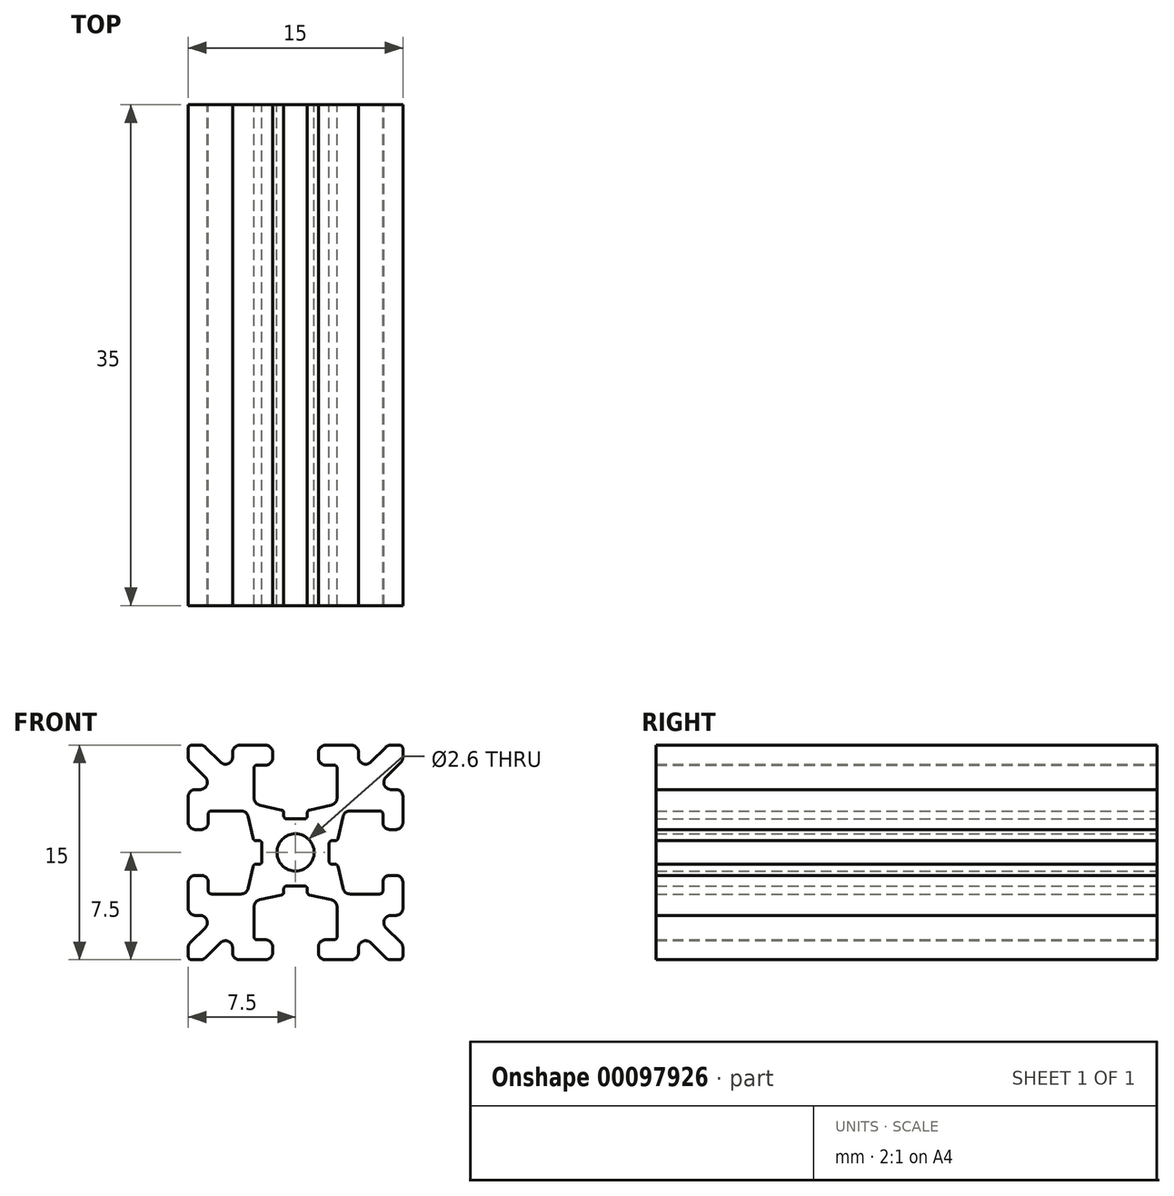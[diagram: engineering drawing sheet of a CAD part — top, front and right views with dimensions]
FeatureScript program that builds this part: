
annotation { "Feature Type Name" : "Feature", "Feature Type Description" : "" }
export const myFeature = defineFeature(function(context is Context, id is Id, definition is map)
    precondition{}
    {
        {
            var Q0;
            Q0=qCreatedBy(makeId("Front.planeOp"),FACE);
            var sketch = newSketch(context, id + "F0", { "sketchPlane" : qUnion([Q0])});
            skLineSegment(sketch, "E0.0.0", {"start": v(0.83, -2.55) * mm, "end": v(0.83, -2.77) * mm});
            skArc(sketch, "E0.0.1", {"start": v(0.83, -2.77) * mm, "mid": v(0.87, -2.9) * mm, "end": v(0.98, -2.97) * mm});
            skLineSegment(sketch, "E0.0.2", {"start": v(0.98, -2.97) * mm, "end": v(2.5, -3.31) * mm});
            skArc(sketch, "E0.0.3", {"start": v(2.5, -3.31) * mm, "mid": v(2.8, -3.49) * mm, "end": v(2.9, -3.8) * mm});
            skLineSegment(sketch, "E0.0.4", {"start": v(2.9, -3.8) * mm, "end": v(2.9, -5.9) * mm});
            skArc(sketch, "E0.0.5", {"start": v(2.9, -5.9) * mm, "mid": v(2.84, -6.04) * mm, "end": v(2.7, -6.1) * mm});
            skLineSegment(sketch, "E0.0.6", {"start": v(2.7, -6.1) * mm, "end": v(2.1, -6.1) * mm});
            skArc(sketch, "E0.0.7", {"start": v(2.1, -6.1) * mm, "mid": v(1.75, -6.25) * mm, "end": v(1.6, -6.6) * mm});
            skLineSegment(sketch, "E0.0.8", {"start": v(1.6, -6.6) * mm, "end": v(1.6, -7) * mm});
            skArc(sketch, "E0.0.9", {"start": v(1.6, -7) * mm, "mid": v(1.75, -7.35) * mm, "end": v(2.1, -7.5) * mm});
            skLineSegment(sketch, "E0.0.10", {"start": v(2.1, -7.5) * mm, "end": v(3.9, -7.5) * mm});
            skArc(sketch, "E0.0.11", {"start": v(3.9, -7.5) * mm, "mid": v(4.25, -7.35) * mm, "end": v(4.4, -7) * mm});
            skLineSegment(sketch, "E0.0.12", {"start": v(4.4, -7) * mm, "end": v(4.4, -6.67) * mm});
            skArc(sketch, "E0.0.13", {"start": v(4.4, -6.67) * mm, "mid": v(4.7, -6.2) * mm, "end": v(5.25, -6.31) * mm});
            skLineSegment(sketch, "E0.0.14", {"start": v(5.25, -6.31) * mm, "end": v(6.3, -7.35) * mm});
            skArc(sketch, "E0.0.15", {"start": v(6.3, -7.35) * mm, "mid": v(6.46, -7.46) * mm, "end": v(6.65, -7.5) * mm});
            skLineSegment(sketch, "E0.0.16", {"start": v(6.65, -7.5) * mm, "end": v(7.25, -7.5) * mm});
            skArc(sketch, "E0.0.17", {"start": v(7.25, -7.5) * mm, "mid": v(7.43, -7.43) * mm, "end": v(7.5, -7.25) * mm});
            skLineSegment(sketch, "E0.0.18", {"start": v(7.5, -7.25) * mm, "end": v(7.5, -6.65) * mm});
            skArc(sketch, "E0.0.19", {"start": v(7.5, -6.65) * mm, "mid": v(7.46, -6.46) * mm, "end": v(7.35, -6.3) * mm});
            skLineSegment(sketch, "E0.0.20", {"start": v(7.35, -6.3) * mm, "end": v(6.31, -5.25) * mm});
            skArc(sketch, "E0.0.21", {"start": v(6.31, -5.25) * mm, "mid": v(6.2, -4.7) * mm, "end": v(6.67, -4.4) * mm});
            skLineSegment(sketch, "E0.0.22", {"start": v(6.67, -4.4) * mm, "end": v(7, -4.4) * mm});
            skArc(sketch, "E0.0.23", {"start": v(7, -4.4) * mm, "mid": v(7.35, -4.25) * mm, "end": v(7.5, -3.9) * mm});
            skLineSegment(sketch, "E0.0.24", {"start": v(7.5, -3.9) * mm, "end": v(7.5, -2.1) * mm});
            skArc(sketch, "E0.0.25", {"start": v(7.5, -2.1) * mm, "mid": v(7.35, -1.75) * mm, "end": v(7, -1.6) * mm});
            skLineSegment(sketch, "E0.0.26", {"start": v(7, -1.6) * mm, "end": v(6.6, -1.6) * mm});
            skArc(sketch, "E0.0.27", {"start": v(6.6, -1.6) * mm, "mid": v(6.25, -1.75) * mm, "end": v(6.1, -2.1) * mm});
            skLineSegment(sketch, "E0.0.28", {"start": v(6.1, -2.1) * mm, "end": v(6.1, -2.7) * mm});
            skArc(sketch, "E0.0.29", {"start": v(6.1, -2.7) * mm, "mid": v(6.04, -2.84) * mm, "end": v(5.9, -2.9) * mm});
            skLineSegment(sketch, "E0.0.30", {"start": v(5.9, -2.9) * mm, "end": v(3.8, -2.9) * mm});
            skArc(sketch, "E0.0.31", {"start": v(3.8, -2.9) * mm, "mid": v(3.49, -2.8) * mm, "end": v(3.31, -2.5) * mm});
            skLineSegment(sketch, "E0.0.32", {"start": v(3.31, -2.5) * mm, "end": v(2.97, -0.98) * mm});
            skArc(sketch, "E0.0.33", {"start": v(2.97, -0.98) * mm, "mid": v(2.9, -0.87) * mm, "end": v(2.77, -0.83) * mm});
            skLineSegment(sketch, "E0.0.34", {"start": v(2.77, -0.83) * mm, "end": v(2.55, -0.83) * mm});
            skArc(sketch, "E0.0.35", {"start": v(2.55, -0.83) * mm, "mid": v(2.4, -0.77) * mm, "end": v(2.35, -0.63) * mm});
            skLineSegment(sketch, "E0.0.36", {"start": v(2.35, -0.63) * mm, "end": v(2.35, 0.63) * mm});
            skArc(sketch, "E0.0.37", {"start": v(2.35, 0.63) * mm, "mid": v(2.4, 0.77) * mm, "end": v(2.55, 0.83) * mm});
            skLineSegment(sketch, "E0.0.38", {"start": v(2.55, 0.83) * mm, "end": v(2.77, 0.83) * mm});
            skArc(sketch, "E0.0.39", {"start": v(2.77, 0.83) * mm, "mid": v(2.9, 0.87) * mm, "end": v(2.97, 0.98) * mm});
            skLineSegment(sketch, "E0.0.40", {"start": v(2.97, 0.98) * mm, "end": v(3.31, 2.5) * mm});
            skArc(sketch, "E0.0.41", {"start": v(3.31, 2.5) * mm, "mid": v(3.49, 2.8) * mm, "end": v(3.8, 2.9) * mm});
            skLineSegment(sketch, "E0.0.42", {"start": v(3.8, 2.9) * mm, "end": v(5.9, 2.9) * mm});
            skArc(sketch, "E0.0.43", {"start": v(5.9, 2.9) * mm, "mid": v(6.04, 2.84) * mm, "end": v(6.1, 2.7) * mm});
            skLineSegment(sketch, "E0.0.44", {"start": v(6.1, 2.7) * mm, "end": v(6.1, 2.1) * mm});
            skArc(sketch, "E0.0.45", {"start": v(6.1, 2.1) * mm, "mid": v(6.25, 1.75) * mm, "end": v(6.6, 1.6) * mm});
            skLineSegment(sketch, "E0.0.46", {"start": v(6.6, 1.6) * mm, "end": v(7, 1.6) * mm});
            skArc(sketch, "E0.0.47", {"start": v(7, 1.6) * mm, "mid": v(7.35, 1.75) * mm, "end": v(7.5, 2.1) * mm});
            skLineSegment(sketch, "E0.0.48", {"start": v(7.5, 2.1) * mm, "end": v(7.5, 3.9) * mm});
            skArc(sketch, "E0.0.49", {"start": v(7.5, 3.9) * mm, "mid": v(7.35, 4.25) * mm, "end": v(7, 4.4) * mm});
            skLineSegment(sketch, "E0.0.50", {"start": v(7, 4.4) * mm, "end": v(6.67, 4.4) * mm});
            skArc(sketch, "E0.0.51", {"start": v(6.67, 4.4) * mm, "mid": v(6.2, 4.7) * mm, "end": v(6.31, 5.25) * mm});
            skLineSegment(sketch, "E0.0.52", {"start": v(6.31, 5.25) * mm, "end": v(7.35, 6.3) * mm});
            skArc(sketch, "E0.0.53", {"start": v(7.35, 6.3) * mm, "mid": v(7.46, 6.46) * mm, "end": v(7.5, 6.65) * mm});
            skLineSegment(sketch, "E0.0.54", {"start": v(7.5, 6.65) * mm, "end": v(7.5, 7.25) * mm});
            skArc(sketch, "E0.0.55", {"start": v(7.5, 7.25) * mm, "mid": v(7.43, 7.43) * mm, "end": v(7.25, 7.5) * mm});
            skLineSegment(sketch, "E0.0.56", {"start": v(7.25, 7.5) * mm, "end": v(6.65, 7.5) * mm});
            skArc(sketch, "E0.0.57", {"start": v(6.65, 7.5) * mm, "mid": v(6.46, 7.46) * mm, "end": v(6.3, 7.35) * mm});
            skLineSegment(sketch, "E0.0.58", {"start": v(6.3, 7.35) * mm, "end": v(5.25, 6.31) * mm});
            skArc(sketch, "E0.0.59", {"start": v(5.25, 6.31) * mm, "mid": v(4.7, 6.2) * mm, "end": v(4.4, 6.67) * mm});
            skLineSegment(sketch, "E0.0.60", {"start": v(4.4, 6.67) * mm, "end": v(4.4, 7) * mm});
            skArc(sketch, "E0.0.61", {"start": v(4.4, 7) * mm, "mid": v(4.25, 7.35) * mm, "end": v(3.9, 7.5) * mm});
            skLineSegment(sketch, "E0.0.62", {"start": v(3.9, 7.5) * mm, "end": v(2.1, 7.5) * mm});
            skArc(sketch, "E0.0.63", {"start": v(2.1, 7.5) * mm, "mid": v(1.75, 7.35) * mm, "end": v(1.6, 7) * mm});
            skLineSegment(sketch, "E0.0.64", {"start": v(1.6, 7) * mm, "end": v(1.6, 6.6) * mm});
            skArc(sketch, "E0.0.65", {"start": v(1.6, 6.6) * mm, "mid": v(1.75, 6.25) * mm, "end": v(2.1, 6.1) * mm});
            skLineSegment(sketch, "E0.0.66", {"start": v(2.1, 6.1) * mm, "end": v(2.7, 6.1) * mm});
            skArc(sketch, "E0.0.67", {"start": v(2.7, 6.1) * mm, "mid": v(2.84, 6.04) * mm, "end": v(2.9, 5.9) * mm});
            skLineSegment(sketch, "E0.0.68", {"start": v(2.9, 5.9) * mm, "end": v(2.9, 3.8) * mm});
            skArc(sketch, "E0.0.69", {"start": v(2.9, 3.8) * mm, "mid": v(2.8, 3.49) * mm, "end": v(2.5, 3.31) * mm});
            skLineSegment(sketch, "E0.0.70", {"start": v(2.5, 3.31) * mm, "end": v(0.98, 2.97) * mm});
            skArc(sketch, "E0.0.71", {"start": v(0.98, 2.97) * mm, "mid": v(0.87, 2.9) * mm, "end": v(0.83, 2.77) * mm});
            skLineSegment(sketch, "E0.0.72", {"start": v(0.83, 2.77) * mm, "end": v(0.83, 2.55) * mm});
            skArc(sketch, "E0.0.73", {"start": v(0.83, 2.55) * mm, "mid": v(0.77, 2.4) * mm, "end": v(0.63, 2.35) * mm});
            skLineSegment(sketch, "E0.0.74", {"start": v(0.63, 2.35) * mm, "end": v(-0.63, 2.35) * mm});
            skArc(sketch, "E0.0.75", {"start": v(-0.63, 2.35) * mm, "mid": v(-0.77, 2.4) * mm, "end": v(-0.83, 2.55) * mm});
            skLineSegment(sketch, "E0.0.76", {"start": v(-0.83, 2.55) * mm, "end": v(-0.83, 2.77) * mm});
            skArc(sketch, "E0.0.77", {"start": v(-0.83, 2.77) * mm, "mid": v(-0.87, 2.9) * mm, "end": v(-0.98, 2.97) * mm});
            skLineSegment(sketch, "E0.0.78", {"start": v(-0.98, 2.97) * mm, "end": v(-2.5, 3.31) * mm});
            skArc(sketch, "E0.0.79", {"start": v(-2.5, 3.31) * mm, "mid": v(-2.8, 3.49) * mm, "end": v(-2.9, 3.8) * mm});
            skLineSegment(sketch, "E0.0.80", {"start": v(-2.9, 3.8) * mm, "end": v(-2.9, 5.9) * mm});
            skArc(sketch, "E0.0.81", {"start": v(-2.9, 5.9) * mm, "mid": v(-2.84, 6.04) * mm, "end": v(-2.7, 6.1) * mm});
            skLineSegment(sketch, "E0.0.82", {"start": v(-2.7, 6.1) * mm, "end": v(-2.1, 6.1) * mm});
            skArc(sketch, "E0.0.83", {"start": v(-2.1, 6.1) * mm, "mid": v(-1.75, 6.25) * mm, "end": v(-1.6, 6.6) * mm});
            skLineSegment(sketch, "E0.0.84", {"start": v(-1.6, 6.6) * mm, "end": v(-1.6, 7) * mm});
            skArc(sketch, "E0.0.85", {"start": v(-1.6, 7) * mm, "mid": v(-1.75, 7.35) * mm, "end": v(-2.1, 7.5) * mm});
            skLineSegment(sketch, "E0.0.86", {"start": v(-2.1, 7.5) * mm, "end": v(-3.9, 7.5) * mm});
            skArc(sketch, "E0.0.87", {"start": v(-3.9, 7.5) * mm, "mid": v(-4.25, 7.35) * mm, "end": v(-4.4, 7) * mm});
            skLineSegment(sketch, "E0.0.88", {"start": v(-4.4, 7) * mm, "end": v(-4.4, 6.67) * mm});
            skArc(sketch, "E0.0.89", {"start": v(-4.4, 6.67) * mm, "mid": v(-4.7, 6.2) * mm, "end": v(-5.25, 6.31) * mm});
            skLineSegment(sketch, "E0.0.90", {"start": v(-5.25, 6.31) * mm, "end": v(-6.3, 7.35) * mm});
            skArc(sketch, "E0.0.91", {"start": v(-6.3, 7.35) * mm, "mid": v(-6.46, 7.46) * mm, "end": v(-6.65, 7.5) * mm});
            skLineSegment(sketch, "E0.0.92", {"start": v(-6.65, 7.5) * mm, "end": v(-7.25, 7.5) * mm});
            skArc(sketch, "E0.0.93", {"start": v(-7.25, 7.5) * mm, "mid": v(-7.43, 7.43) * mm, "end": v(-7.5, 7.25) * mm});
            skLineSegment(sketch, "E0.0.94", {"start": v(-7.5, 7.25) * mm, "end": v(-7.5, 6.65) * mm});
            skArc(sketch, "E0.0.95", {"start": v(-7.5, 6.65) * mm, "mid": v(-7.46, 6.46) * mm, "end": v(-7.35, 6.3) * mm});
            skLineSegment(sketch, "E0.0.96", {"start": v(-7.35, 6.3) * mm, "end": v(-6.31, 5.25) * mm});
            skArc(sketch, "E0.0.97", {"start": v(-6.31, 5.25) * mm, "mid": v(-6.2, 4.7) * mm, "end": v(-6.67, 4.4) * mm});
            skLineSegment(sketch, "E0.0.98", {"start": v(-6.67, 4.4) * mm, "end": v(-7, 4.4) * mm});
            skArc(sketch, "E0.0.99", {"start": v(-7, 4.4) * mm, "mid": v(-7.35, 4.25) * mm, "end": v(-7.5, 3.9) * mm});
            skLineSegment(sketch, "E0.0.100", {"start": v(-7.5, 3.9) * mm, "end": v(-7.5, 2.1) * mm});
            skArc(sketch, "E0.0.101", {"start": v(-7.5, 2.1) * mm, "mid": v(-7.35, 1.75) * mm, "end": v(-7, 1.6) * mm});
            skLineSegment(sketch, "E0.0.102", {"start": v(-7, 1.6) * mm, "end": v(-6.6, 1.6) * mm});
            skArc(sketch, "E0.0.103", {"start": v(-6.6, 1.6) * mm, "mid": v(-6.25, 1.75) * mm, "end": v(-6.1, 2.1) * mm});
            skLineSegment(sketch, "E0.0.104", {"start": v(-6.1, 2.1) * mm, "end": v(-6.1, 2.7) * mm});
            skArc(sketch, "E0.0.105", {"start": v(-6.1, 2.7) * mm, "mid": v(-6.04, 2.84) * mm, "end": v(-5.9, 2.9) * mm});
            skLineSegment(sketch, "E0.0.106", {"start": v(-5.9, 2.9) * mm, "end": v(-3.8, 2.9) * mm});
            skArc(sketch, "E0.0.107", {"start": v(-3.8, 2.9) * mm, "mid": v(-3.49, 2.8) * mm, "end": v(-3.31, 2.5) * mm});
            skLineSegment(sketch, "E0.0.108", {"start": v(-3.31, 2.5) * mm, "end": v(-2.97, 0.98) * mm});
            skArc(sketch, "E0.0.109", {"start": v(-2.97, 0.98) * mm, "mid": v(-2.9, 0.87) * mm, "end": v(-2.77, 0.83) * mm});
            skLineSegment(sketch, "E0.0.110", {"start": v(-2.77, 0.83) * mm, "end": v(-2.55, 0.83) * mm});
            skArc(sketch, "E0.0.111", {"start": v(-2.55, 0.83) * mm, "mid": v(-2.4, 0.77) * mm, "end": v(-2.35, 0.63) * mm});
            skLineSegment(sketch, "E0.0.112", {"start": v(-2.35, 0.63) * mm, "end": v(-2.35, -0.63) * mm});
            skArc(sketch, "E0.0.113", {"start": v(-2.35, -0.63) * mm, "mid": v(-2.4, -0.77) * mm, "end": v(-2.55, -0.83) * mm});
            skLineSegment(sketch, "E0.0.114", {"start": v(-2.55, -0.83) * mm, "end": v(-2.77, -0.83) * mm});
            skArc(sketch, "E0.0.115", {"start": v(-2.77, -0.83) * mm, "mid": v(-2.9, -0.87) * mm, "end": v(-2.97, -0.98) * mm});
            skLineSegment(sketch, "E0.0.116", {"start": v(-2.97, -0.98) * mm, "end": v(-3.31, -2.5) * mm});
            skArc(sketch, "E0.0.117", {"start": v(-3.31, -2.5) * mm, "mid": v(-3.49, -2.8) * mm, "end": v(-3.8, -2.9) * mm});
            skLineSegment(sketch, "E0.0.118", {"start": v(-3.8, -2.9) * mm, "end": v(-5.9, -2.9) * mm});
            skArc(sketch, "E0.0.119", {"start": v(-5.9, -2.9) * mm, "mid": v(-6.04, -2.84) * mm, "end": v(-6.1, -2.7) * mm});
            skLineSegment(sketch, "E0.0.120", {"start": v(-6.1, -2.7) * mm, "end": v(-6.1, -2.1) * mm});
            skArc(sketch, "E0.0.121", {"start": v(-6.1, -2.1) * mm, "mid": v(-6.25, -1.75) * mm, "end": v(-6.6, -1.6) * mm});
            skLineSegment(sketch, "E0.0.122", {"start": v(-6.6, -1.6) * mm, "end": v(-7, -1.6) * mm});
            skArc(sketch, "E0.0.123", {"start": v(-7, -1.6) * mm, "mid": v(-7.35, -1.75) * mm, "end": v(-7.5, -2.1) * mm});
            skLineSegment(sketch, "E0.0.124", {"start": v(-7.5, -2.1) * mm, "end": v(-7.5, -3.9) * mm});
            skArc(sketch, "E0.0.125", {"start": v(-7.5, -3.9) * mm, "mid": v(-7.35, -4.25) * mm, "end": v(-7, -4.4) * mm});
            skLineSegment(sketch, "E0.0.126", {"start": v(-7, -4.4) * mm, "end": v(-6.67, -4.4) * mm});
            skArc(sketch, "E0.0.127", {"start": v(-6.67, -4.4) * mm, "mid": v(-6.2, -4.7) * mm, "end": v(-6.31, -5.25) * mm});
            skLineSegment(sketch, "E0.0.128", {"start": v(-6.31, -5.25) * mm, "end": v(-7.35, -6.3) * mm});
            skArc(sketch, "E0.0.129", {"start": v(-7.35, -6.3) * mm, "mid": v(-7.46, -6.46) * mm, "end": v(-7.5, -6.65) * mm});
            skLineSegment(sketch, "E0.0.130", {"start": v(-7.5, -6.65) * mm, "end": v(-7.5, -7.25) * mm});
            skArc(sketch, "E0.0.131", {"start": v(-7.5, -7.25) * mm, "mid": v(-7.43, -7.43) * mm, "end": v(-7.25, -7.5) * mm});
            skLineSegment(sketch, "E0.0.132", {"start": v(-7.25, -7.5) * mm, "end": v(-6.65, -7.5) * mm});
            skArc(sketch, "E0.0.133", {"start": v(-6.65, -7.5) * mm, "mid": v(-6.46, -7.46) * mm, "end": v(-6.3, -7.35) * mm});
            skLineSegment(sketch, "E0.0.134", {"start": v(-6.3, -7.35) * mm, "end": v(-5.25, -6.31) * mm});
            skArc(sketch, "E0.0.135", {"start": v(-5.25, -6.31) * mm, "mid": v(-4.7, -6.2) * mm, "end": v(-4.4, -6.67) * mm});
            skLineSegment(sketch, "E0.0.136", {"start": v(-4.4, -6.67) * mm, "end": v(-4.4, -7) * mm});
            skArc(sketch, "E0.0.137", {"start": v(-4.4, -7) * mm, "mid": v(-4.25, -7.35) * mm, "end": v(-3.9, -7.5) * mm});
            skLineSegment(sketch, "E0.0.138", {"start": v(-3.9, -7.5) * mm, "end": v(-2.1, -7.5) * mm});
            skArc(sketch, "E0.0.139", {"start": v(-2.1, -7.5) * mm, "mid": v(-1.75, -7.35) * mm, "end": v(-1.6, -7) * mm});
            skLineSegment(sketch, "E0.0.140", {"start": v(-1.6, -7) * mm, "end": v(-1.6, -6.6) * mm});
            skArc(sketch, "E0.0.141", {"start": v(-1.6, -6.6) * mm, "mid": v(-1.75, -6.25) * mm, "end": v(-2.1, -6.1) * mm});
            skLineSegment(sketch, "E0.0.142", {"start": v(-2.1, -6.1) * mm, "end": v(-2.7, -6.1) * mm});
            skArc(sketch, "E0.0.143", {"start": v(-2.7, -6.1) * mm, "mid": v(-2.84, -6.04) * mm, "end": v(-2.9, -5.9) * mm});
            skLineSegment(sketch, "E0.0.144", {"start": v(-2.9, -5.9) * mm, "end": v(-2.9, -3.8) * mm});
            skArc(sketch, "E0.0.145", {"start": v(-2.9, -3.8) * mm, "mid": v(-2.8, -3.49) * mm, "end": v(-2.5, -3.31) * mm});
            skLineSegment(sketch, "E0.0.146", {"start": v(-2.5, -3.31) * mm, "end": v(-0.98, -2.97) * mm});
            skArc(sketch, "E0.0.147", {"start": v(-0.98, -2.97) * mm, "mid": v(-0.87, -2.9) * mm, "end": v(-0.83, -2.77) * mm});
            skLineSegment(sketch, "E0.0.148", {"start": v(-0.83, -2.77) * mm, "end": v(-0.83, -2.55) * mm});
            skArc(sketch, "E0.0.149", {"start": v(-0.83, -2.55) * mm, "mid": v(-0.77, -2.4) * mm, "end": v(-0.63, -2.35) * mm});
            skLineSegment(sketch, "E0.0.150", {"start": v(-0.63, -2.35) * mm, "end": v(0.63, -2.35) * mm});
            skArc(sketch, "E0.0.151", {"start": v(0.63, -2.35) * mm, "mid": v(0.77, -2.4) * mm, "end": v(0.83, -2.55) * mm});
            skPoint(sketch, "E1", {"position": v(0, 0) * mm});
            skPoint(sketch, "E1.positionSnap0", {"position": v(0, 2.35) * mm});
            skPoint(sketch, "E1.positionSnap1", {"position": v(2.35, 0) * mm});
            skCircle(sketch, "E2", {"center": v(0, 0) * mm, "radius": 1.3 * mm});
            skSolve(sketch);
        }
        {
            var Q0;
            Q0=makeQuery(id+"F0.imprint","IMPRINT",FACE,{"disambiguationData":[TD([[makeQuery(id+"F0.imprint","IMPRINT",EDGE,{"derivedFrom":sQuery(id+"F0.wireOp",EDGE,"E0.0.0")}),1.0]])]});
            extrude(context, id + "F1", {"entities" : qUnion([Q0]), "endBound" : BoundingType.SYMMETRIC, "depth" : 35 * mm});
        }
    });
